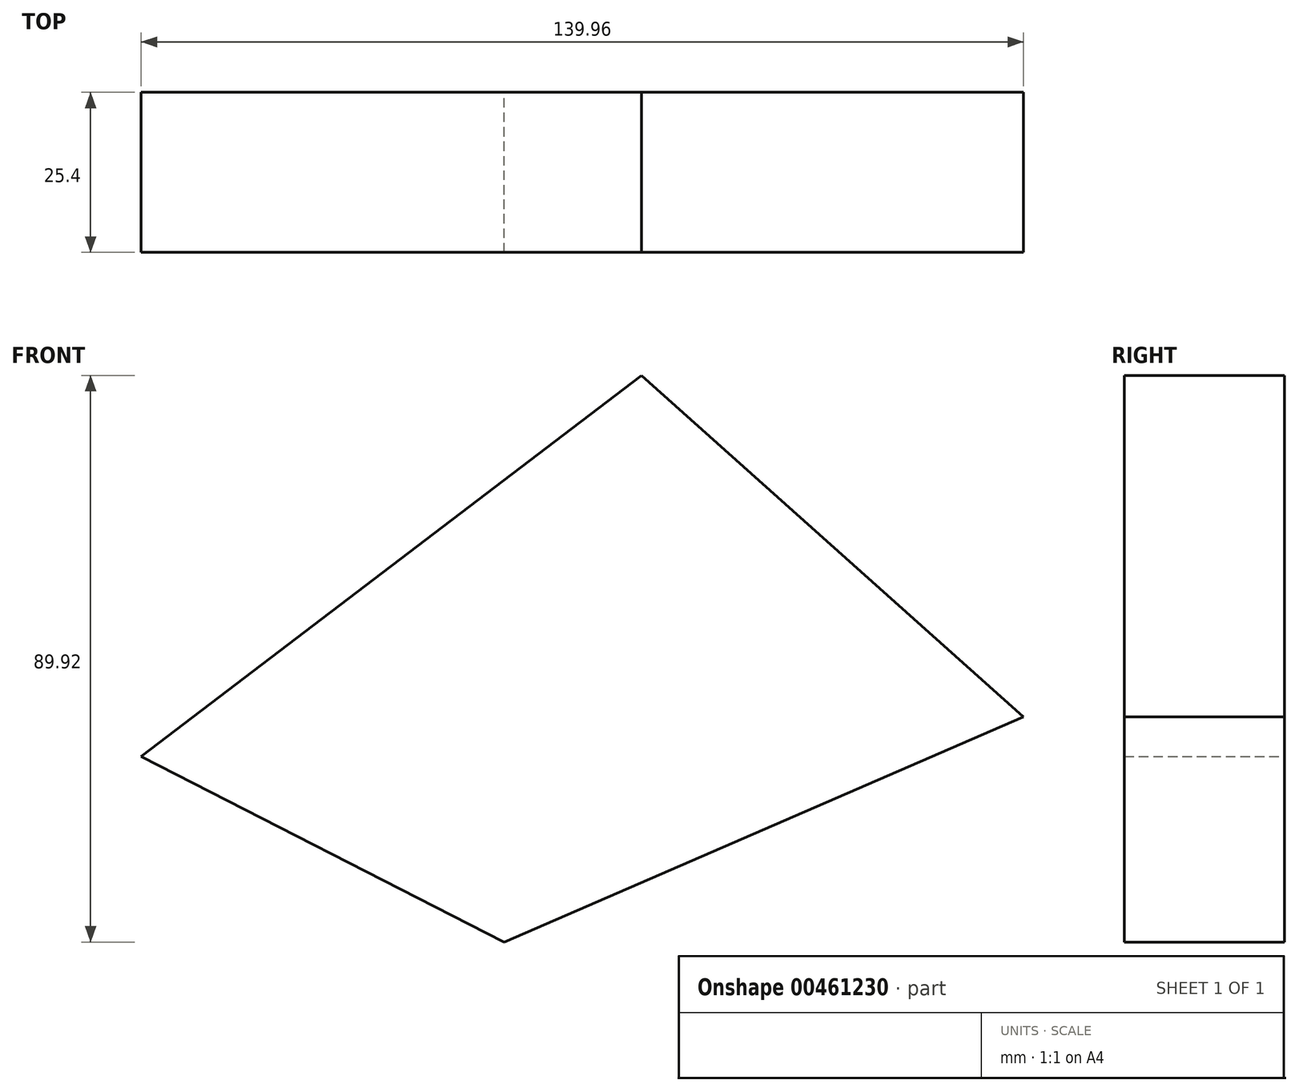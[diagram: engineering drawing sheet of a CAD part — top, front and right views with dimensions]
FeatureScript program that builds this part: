
annotation { "Feature Type Name" : "Feature", "Feature Type Description" : "" }
export const myFeature = defineFeature(function(context is Context, id is Id, definition is map)
    precondition{}
    {
        {
            var Q0;
            Q0=qCreatedBy(makeId("Front.planeOp"),FACE);
            var sketch = newSketch(context, id + "F0", { "sketchPlane" : qUnion([Q0])});
            skLineSegment(sketch, "E0", {"start": v(0, 0) * mm, "end": v(60.6, -54.2) * mm});
            skLineSegment(sketch, "E1", {"start": v(60.6, -54.2) * mm, "end": v(-21.76, -89.92) * mm});
            skLineSegment(sketch, "E2", {"start": v(-21.76, -89.92) * mm, "end": v(-79.37, -60.46) * mm});
            skLineSegment(sketch, "E3", {"start": v(-79.37, -60.46) * mm, "end": v(0, 0) * mm});
            skSolve(sketch);
        }
        {
            var Q0;
            Q0=makeQuery(id+"F0.imprint","IMPRINT",FACE,{"disambiguationData":[TD([[makeQuery(id+"F0.imprint","IMPRINT",EDGE,{"derivedFrom":sQuery(id+"F0.wireOp",EDGE,"E0")}),-1.0]])]});
            extrude(context, id + "F1", {"entities" : qUnion([Q0]), "depth" : 25.4 * mm});
        }
    });
